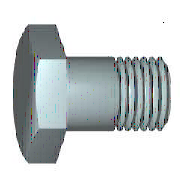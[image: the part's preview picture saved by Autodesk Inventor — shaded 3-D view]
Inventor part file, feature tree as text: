
AUTODESK INVENTOR PART (.ipt)
format: ipt  version: 2014 SP1 (Build 180222100, 222)  size: 189,440 bytes
history: native  units: mm (DEFAULTED — no unit token found)
features: sketch x2, extrude x1, chamfer x1, fillet x1, plane x1
ambient origin geometry x7: Origin, YZ Plane, XZ Plane, X Axis, Y Axis, Z Axis, Center Point
bodies: Solid1 (feature_tree), Body (feature_tree)
feature tree (6):
  extrude  "Head"  TaperAngle=90.0deg  [1 undecoded]
  chamfer  "Chamfer1"  [1 undecoded]
  fillet  "Fillet2"  [1 undecoded]
  plane  "Work Plane1"
  sketch  "Sketch1"  dims[d2=6.0mm d12=90.0deg]
  sketch  "Sketch2"  dims[d3=4.0mm d4=0.0mm d21=90.0deg d6=0.61345mm d7=0.61355mm d8=0.0mm d11=10.0mm d15=15.0mm d16=0.0mm d55=45.0deg d58=0.0mm d59=16.0mm d65=10.0mm d67=30.0deg d68=12.0mm d69=4.0mm d71=0.25mm d73=0.0mm]
note: 3 required parameter values undecoded (feature->parameter linkage not recoverable at this tier; creation-order binding heuristic only, values carry confidence <= 0.55)
